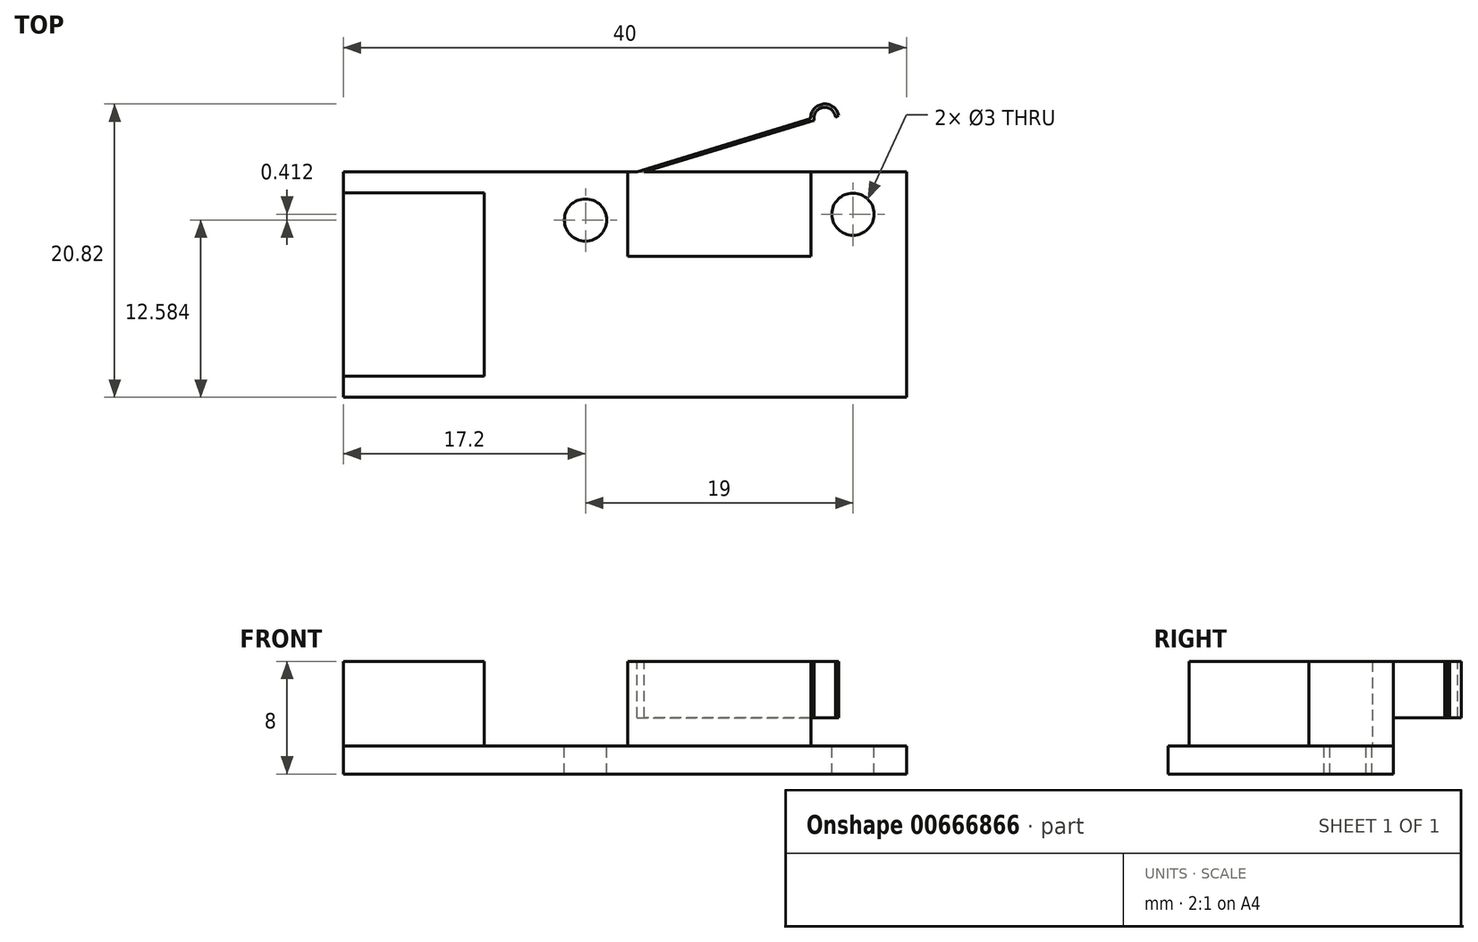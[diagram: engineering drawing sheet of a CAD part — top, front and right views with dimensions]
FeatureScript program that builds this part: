
annotation { "Feature Type Name" : "Feature", "Feature Type Description" : "" }
export const myFeature = defineFeature(function(context is Context, id is Id, definition is map)
    precondition{}
    {
        {
            var Q0;
            Q0=qCreatedBy(makeId("Top.planeOp"),FACE);
            var sketch = newSketch(context, id + "F0", { "sketchPlane" : qUnion([Q0])});
            skLineSegment(sketch, "E0.bottom", {"start": v(0, 0) * mm, "end": v(40, 0) * mm});
            skLineSegment(sketch, "E0.top", {"start": v(0, 16) * mm, "end": v(40, 16) * mm});
            skLineSegment(sketch, "E0.left", {"start": v(0, 0) * mm, "end": v(0, 16) * mm});
            skLineSegment(sketch, "E0.right", {"start": v(40, 0) * mm, "end": v(40, 16) * mm});
            skSolve(sketch);
        }
        {
            var Q0;
            Q0=makeQuery(id+"F0.imprint","IMPRINT",FACE,{"disambiguationData":[TD([[makeQuery(id+"F0.imprint","IMPRINT",EDGE,{"derivedFrom":sQuery(id+"F0.wireOp",EDGE,"E0.bottom")}),1.0]])]});
            extrude(context, id + "F1", {"entities" : qUnion([Q0]), "depth" : 2 * mm, "offsetDistance" : 25 * mm});
        }
        {
            var Q0;
            Q0=makeQuery(id+"F1.opExtrude","CAP_FACE",FACE,{"disambiguationData":[OSD([sQuery(id+"F0.wireOp",EDGE,"E0.bottom"),sQuery(id+"F0.wireOp",EDGE,"E0.top"),sQuery(id+"F0.wireOp",EDGE,"E0.left"),sQuery(id+"F0.wireOp",EDGE,"E0.right")])],"isStart":false});
            var sketch = newSketch(context, id + "F2", { "sketchPlane" : qUnion([Q0])});
            skLineSegment(sketch, "E1.bottom", {"start": v(0, 14.5) * mm, "end": v(10, 14.5) * mm});
            skLineSegment(sketch, "E1.top", {"start": v(0, 1.5) * mm, "end": v(10, 1.5) * mm});
            skLineSegment(sketch, "E1.left", {"start": v(0, 14.5) * mm, "end": v(0, 1.5) * mm});
            skLineSegment(sketch, "E1.right", {"start": v(10, 14.5) * mm, "end": v(10, 1.5) * mm});
            skLineSegment(sketch, "E2", {"start": v(-3.52, 8) * mm, "end": v(26.42, 8) * mm, "construction": true});
            skLineSegment(sketch, "E3.bottom", {"start": v(33.2, 16) * mm, "end": v(20.2, 16) * mm});
            skLineSegment(sketch, "E3.top", {"start": v(33.2, 10) * mm, "end": v(20.2, 10) * mm});
            skLineSegment(sketch, "E3.left", {"start": v(33.2, 16) * mm, "end": v(33.2, 10) * mm});
            skLineSegment(sketch, "E3.right", {"start": v(20.2, 16) * mm, "end": v(20.2, 10) * mm});
            skSolve(sketch);
        }
        {
            var Q0;
            Q0 = qSketchRegion(id + "F2", true);
            extrude(context, id + "F3", {"entities" : qUnion([Q0]), "operationType" : NewBodyOperationType.ADD, "depth" : 6 * mm, "offsetDistance" : 25 * mm});
        }
        {
            var Q0;
            Q0=makeQuery(id+"F1.opExtrude","CAP_FACE",FACE,{"disambiguationData":[OSD([sQuery(id+"F0.wireOp",EDGE,"E0.bottom"),sQuery(id+"F0.wireOp",EDGE,"E0.top"),sQuery(id+"F0.wireOp",EDGE,"E0.left"),sQuery(id+"F0.wireOp",EDGE,"E0.right")])],"isStart":false});
            var sketch = newSketch(context, id + "F4", { "sketchPlane" : qUnion([Q0])});
            skCircle(sketch, "E4", {"center": v(17.2, 12.58) * mm, "radius": 1.5 * mm});
            skCircle(sketch, "E5", {"center": v(36.2, 13) * mm, "radius": 1.5 * mm});
            skSolve(sketch);
        }
        {
            var Q0;
            Q0 = qSketchRegion(id + "F4", true);
            extrude(context, id + "F5", {"entities" : qUnion([Q0]), "operationType" : NewBodyOperationType.REMOVE, "oppositeDirection" : true, "depth" : 25 * mm, "offsetDistance" : 25 * mm});
        }
        {
            var Q0;
            Q0=makeQuery(id+"F3.opExtrude","CAP_FACE",FACE,{"disambiguationData":[OSD([sQuery(id+"F2.wireOp",EDGE,"E3.bottom"),sQuery(id+"F2.wireOp",EDGE,"E3.top"),sQuery(id+"F2.wireOp",EDGE,"E3.left"),sQuery(id+"F2.wireOp",EDGE,"E3.right")])],"isStart":false});
            var sketch = newSketch(context, id + "F6", { "sketchPlane" : qUnion([Q0])});
            skLineSegment(sketch, "E6", {"start": v(20.87, 16) * mm, "end": v(33.2, 19.8) * mm});
            skArc(sketch, "E7", {"start": v(35.18, 20) * mm, "mid": v(34.1, 20.82) * mm, "end": v(33.2, 19.8) * mm});
            skArc(sketch, "E8", {"start": v(34.96, 19.88) * mm, "mid": v(34.1, 20.58) * mm, "end": v(33.45, 19.67) * mm});
            skLineSegment(sketch, "E9", {"start": v(34.96, 19.88) * mm, "end": v(35.18, 20) * mm});
            skLineSegment(sketch, "E10", {"start": v(33.45, 19.67) * mm, "end": v(21.37, 16) * mm});
            skLineSegment(sketch, "E11", {"start": v(21.37, 16) * mm, "end": v(20.87, 16) * mm});
            skSolve(sketch);
        }
        {
            var Q0;
            Q0=makeQuery(id+"F6.imprint","IMPRINT",FACE,{"disambiguationData":[TD([[makeQuery(id+"F6.imprint","IMPRINT",EDGE,{"derivedFrom":sQuery(id+"F6.wireOp",EDGE,"E6")}),-1.0]])]});
            var Q1;
            Q1=makeQuery(id+"F1.opExtrude","CAP_FACE",FACE,{"disambiguationData":[OSD([sQuery(id+"F0.wireOp",EDGE,"E0.bottom"),sQuery(id+"F0.wireOp",EDGE,"E0.top"),sQuery(id+"F0.wireOp",EDGE,"E0.left"),sQuery(id+"F0.wireOp",EDGE,"E0.right")])],"isStart":true});
            extrude(context, id + "F7", {"entities" : qUnion([Q0]), "operationType" : NewBodyOperationType.ADD, "oppositeDirection" : true, "depth" : 4 * mm, "endBoundEntityFace" : qUnion([Q1]), "offsetDistance" : 25 * mm});
        }
    });
